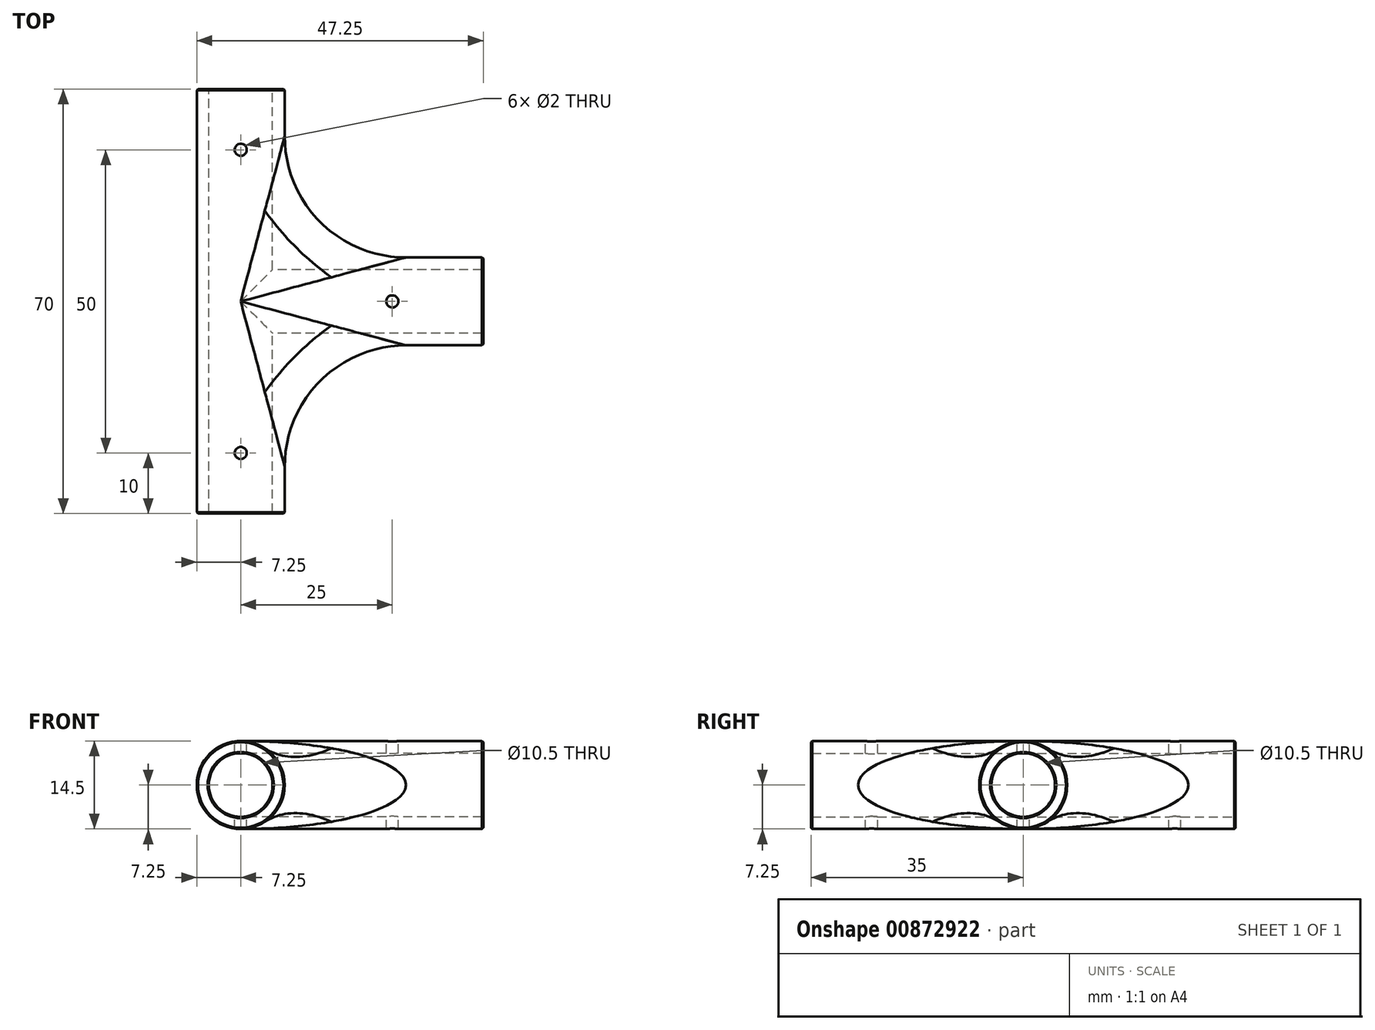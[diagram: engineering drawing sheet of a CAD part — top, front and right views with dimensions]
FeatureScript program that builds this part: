
annotation { "Feature Type Name" : "Feature", "Feature Type Description" : "" }
export const myFeature = defineFeature(function(context is Context, id is Id, definition is map)
    precondition{}
    {
        {
            var Q0;
            Q0=qCreatedBy(makeId("Front.planeOp"),FACE);
            var sketch = newSketch(context, id + "F0", { "sketchPlane" : qUnion([Q0])});
            skCircle(sketch, "E0", {"center": v(0, 0) * mm, "radius": 7.25 * mm});
            skCircle(sketch, "E1", {"center": v(0, 0) * mm, "radius": 5.25 * mm});
            skSolve(sketch);
        }
        {
            var Q0;
            Q0=qSketchRegion(id+"F0",true);
            extrude(context, id + "F1", {"entities" : qUnion([Q0]), "endBound" : BoundingType.SYMMETRIC, "depth" : 70 * mm, "offsetDistance" : 25 * mm});
        }
        {
            var Q0;
            Q0=qCreatedBy(makeId("Right.planeOp"),FACE);
            var sketch = newSketch(context, id + "F2", { "sketchPlane" : qUnion([Q0])});
            skCircle(sketch, "E2", {"center": v(0, 0) * mm, "radius": 7.25 * mm});
            skCircle(sketch, "E3", {"center": v(0, 0) * mm, "radius": 5.25 * mm});
            skSolve(sketch);
        }
        {
            var Q0;
            Q0=qSketchRegion(id+"F2",true);
            extrude(context, id + "F3", {"entities" : qUnion([Q0]), "operationType" : NewBodyOperationType.ADD, "depth" : 40 * mm, "offsetDistance" : 25 * mm});
        }
        {
            var Q0;
            Q0=makeQuery(id+"F0.imprint","IMPRINT",FACE,{"disambiguationData":[TD([[makeQuery(id+"F0.imprint","IMPRINT",EDGE,{"derivedFrom":sQuery(id+"F0.wireOp",EDGE,"E1")}),1.0]])]});
            extrude(context, id + "F4", {"entities" : qUnion([Q0]), "operationType" : NewBodyOperationType.REMOVE, "endBound" : BoundingType.THROUGH_ALL, "oppositeDirection" : true, "depth" : 25 * mm, "offsetDistance" : 25 * mm, "hasSecondDirection" : true, "secondDirectionBound" : SecondDirectionBoundingType.THROUGH_ALL, "secondDirectionOppositeDirection" : false, "secondDirectionDepth" : 25 * mm});
        }
        {
            var Q0;
            Q0=makeQuery(id+"F2.imprint","IMPRINT",FACE,{"disambiguationData":[TD([[makeQuery(id+"F2.imprint","IMPRINT",EDGE,{"derivedFrom":sQuery(id+"F2.wireOp",EDGE,"E3")}),1.0]])]});
            extrude(context, id + "F5", {"entities" : qUnion([Q0]), "operationType" : NewBodyOperationType.REMOVE, "endBound" : BoundingType.THROUGH_ALL, "depth" : 25 * mm, "offsetDistance" : 25 * mm});
        }
        {
            var Q0;
            Q0=makeQuery(id+"F3.boolean.opBoolean","INTERSECT",EDGE,{"disambiguationData":[OD(0.0)],"derivedFrom":[makeQuery(id+"F1.opExtrude","SWEPT_FACE",FACE,{"disambiguationData":[OSD([sQuery(id+"F0.wireOp",EDGE,"E0")])]}),makeQuery(id+"F3.opExtrude","SWEPT_FACE",FACE,{"disambiguationData":[OSD([sQuery(id+"F2.wireOp",EDGE,"E2")])]})]});
            var Q1;
            Q1=makeQuery(id+"F3.boolean.opBoolean","INTERSECT",EDGE,{"disambiguationData":[OD(1.0)],"derivedFrom":[makeQuery(id+"F1.opExtrude","SWEPT_FACE",FACE,{"disambiguationData":[OSD([sQuery(id+"F0.wireOp",EDGE,"E0")])]}),makeQuery(id+"F3.opExtrude","SWEPT_FACE",FACE,{"disambiguationData":[OSD([sQuery(id+"F2.wireOp",EDGE,"E2")])]})]});
            fillet(context, id + "F6", {"entities" : qUnion([Q0, Q1]), "radius" : 20 * mm, "tangentPropagation" : true, "allowEdgeOverflow" : false});
        }
        {
            var Q0;
            Q0=makeQuery(id+"F1.opExtrude","CAP_FACE",FACE,{"disambiguationData":[OSD([sQuery(id+"F0.wireOp",EDGE,"E0"),sQuery(id+"F0.wireOp",EDGE,"E1")])],"isStart":false});
            var Q1;
            Q1=makeQuery(id+"F3.opExtrude","CAP_FACE",FACE,{"disambiguationData":[OSD([sQuery(id+"F2.wireOp",EDGE,"E2"),sQuery(id+"F2.wireOp",EDGE,"E3")])],"isStart":false});
            var Q2;
            Q2=makeQuery(id+"F1.opExtrude","CAP_FACE",FACE,{"disambiguationData":[OSD([sQuery(id+"F0.wireOp",EDGE,"E0"),sQuery(id+"F0.wireOp",EDGE,"E1")])],"isStart":true});
            chamfer(context, id + "F7", {"entities" : qUnion([Q0, Q1, Q2]), "width" : 0.2 * mm, "tangentPropagation" : true});
        }
        {
            var Q0;
            Q0=qCreatedBy(makeId("Top.planeOp"),FACE);
            var sketch = newSketch(context, id + "F8", { "sketchPlane" : qUnion([Q0])});
            skLineSegment(sketch, "E4", {"start": v(0, 37.68) * mm, "end": v(0, -40.37) * mm, "construction": true});
            skLineSegment(sketch, "E5", {"start": v(40, 0) * mm, "end": v(-21.32, 0) * mm, "construction": true});
            skCircle(sketch, "E6", {"center": v(0, 25) * mm, "radius": 1 * mm});
            skCircle(sketch, "E7", {"center": v(25, 0) * mm, "radius": 1 * mm});
            skCircle(sketch, "E8", {"center": v(0, -25) * mm, "radius": 1 * mm});
            skSolve(sketch);
        }
        {
            var Q0;
            Q0=qSketchRegion(id+"F8",true);
            extrude(context, id + "F9", {"entities" : qUnion([Q0]), "operationType" : NewBodyOperationType.REMOVE, "endBound" : BoundingType.THROUGH_ALL, "oppositeDirection" : true, "depth" : 25 * mm, "offsetDistance" : 25 * mm, "hasSecondDirection" : true, "secondDirectionBound" : SecondDirectionBoundingType.THROUGH_ALL, "secondDirectionOppositeDirection" : false, "secondDirectionDepth" : 25 * mm});
        }
    });
